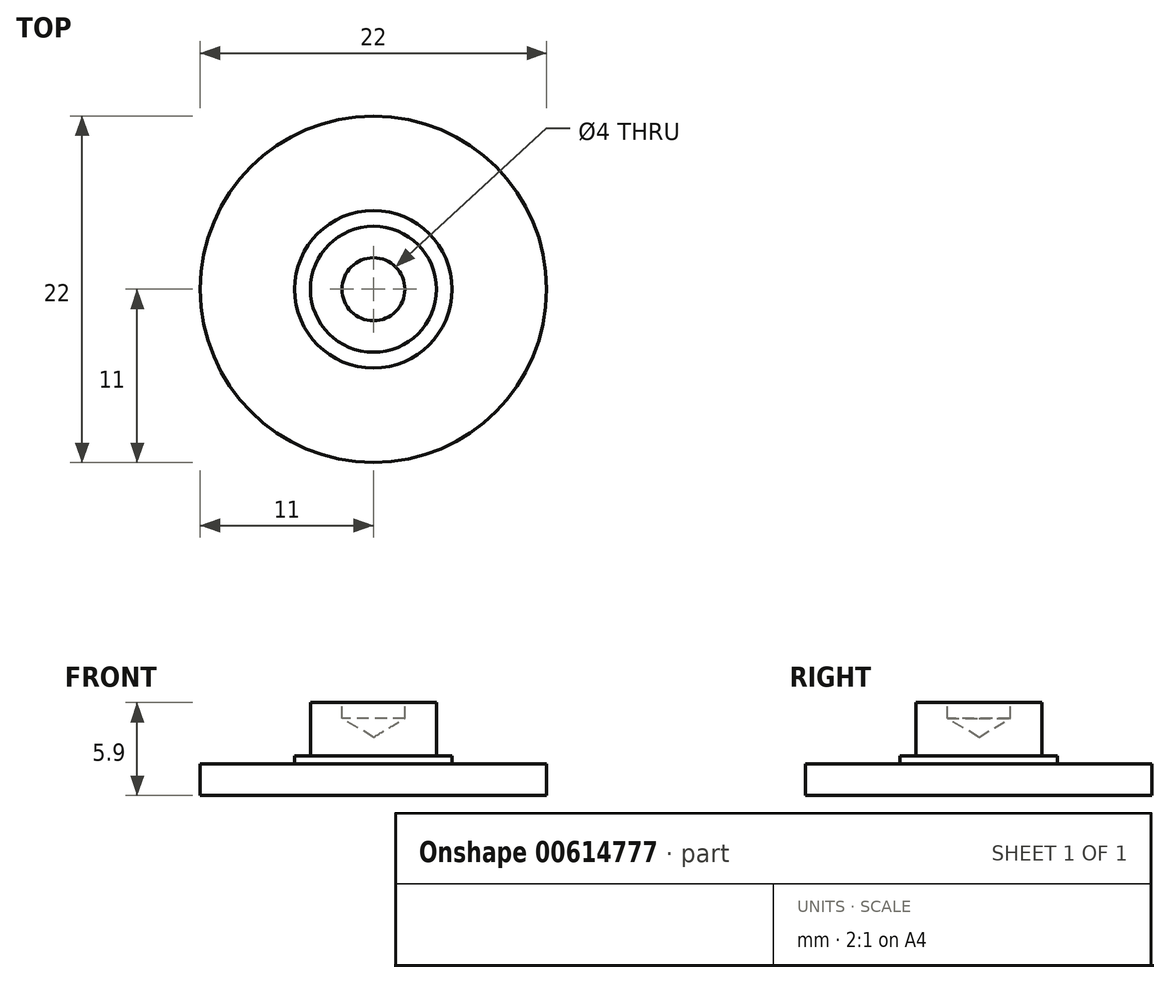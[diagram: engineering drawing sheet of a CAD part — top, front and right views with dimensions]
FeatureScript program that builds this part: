
annotation { "Feature Type Name" : "Feature", "Feature Type Description" : "" }
export const myFeature = defineFeature(function(context is Context, id is Id, definition is map)
    precondition{}
    {
        {
            var Q0;
            Q0=qCreatedBy(makeId("Top.planeOp"),FACE);
            var sketch = newSketch(context, id + "F0", { "sketchPlane" : qUnion([Q0])});
            skCircle(sketch, "E0", {"center": v(0, 0) * mm, "radius": 11 * mm});
            skSolve(sketch);
        }
        {
            var Q0;
            Q0=makeQuery(id+"F0.imprint","IMPRINT",FACE,{"disambiguationData":[TD([[makeQuery(id+"F0.imprint","IMPRINT",EDGE,{"derivedFrom":sQuery(id+"F0.wireOp",EDGE,"E0")}),1.0]])]});
            extrude(context, id + "F1", {"entities" : qUnion([Q0]), "depth" : 2 * mm, "offsetDistance" : 25 * mm});
        }
        {
            var Q0;
            Q0=makeQuery(id+"F1.opExtrude","CAP_FACE",FACE,{"disambiguationData":[OSD([sQuery(id+"F0.wireOp",EDGE,"E0")])],"isStart":false});
            var sketch = newSketch(context, id + "F2", { "sketchPlane" : qUnion([Q0])});
            skCircle(sketch, "E1", {"center": v(0, 0) * mm, "radius": 5 * mm});
            skSolve(sketch);
        }
        {
            var Q0;
            Q0=makeQuery(id+"F2.imprint","IMPRINT",FACE,{"disambiguationData":[TD([[makeQuery(id+"F2.imprint","IMPRINT",EDGE,{"derivedFrom":sQuery(id+"F2.wireOp",EDGE,"E1")}),1.0]])]});
            extrude(context, id + "F3", {"entities" : qUnion([Q0]), "operationType" : NewBodyOperationType.ADD, "depth" : 0.5 * mm, "offsetDistance" : 25 * mm});
        }
        {
            var Q0;
            Q0=makeQuery(id+"F3.opExtrude","CAP_FACE",FACE,{"disambiguationData":[OSD([sQuery(id+"F2.wireOp",EDGE,"E1")])],"isStart":false});
            var sketch = newSketch(context, id + "F4", { "sketchPlane" : qUnion([Q0])});
            skCircle(sketch, "E2", {"center": v(0, 0) * mm, "radius": 4 * mm});
            skSolve(sketch);
        }
        {
            var Q0;
            Q0=makeQuery(id+"F4.imprint","IMPRINT",FACE,{"disambiguationData":[TD([[makeQuery(id+"F4.imprint","IMPRINT",EDGE,{"derivedFrom":sQuery(id+"F4.wireOp",EDGE,"E2")}),1.0]])]});
            extrude(context, id + "F5", {"entities" : qUnion([Q0]), "operationType" : NewBodyOperationType.ADD, "depth" : 3.4 * mm, "offsetDistance" : 25 * mm});
        }
        {
            var Q0;
            Q0=makeQuery(id+"F5.opExtrude","CAP_FACE",FACE,{"disambiguationData":[OSD([sQuery(id+"F4.wireOp",EDGE,"E2")])],"isStart":false});
            var sketch = newSketch(context, id + "F6", { "sketchPlane" : qUnion([Q0])});
            skPoint(sketch, "E3", {"position": v(0, 0) * mm});
            skSolve(sketch);
        }
        {
            var Q0;
            Q0=sQuery(id+"F6.wireOp",VERTEX,"E3");
            var Q1;
            Q1=makeQuery(id+"F1.opExtrude","SWEPT_BODY",BODY,{"disambiguationData":[OSD([sQuery(id+"F0.wireOp",EDGE,"E0")])]});
            hole(context, id + "F7", {"style" : HoleStyle.SIMPLE, "endStyle" : HoleEndStyle.BLIND, "holeDiameter" : 4 * mm, "majorDiameter" : 5 * mm, "holeDepth" : 1 * mm, "isTappedThrough" : true, "tappedDepth" : 12 * mm, "tapClearance" : 3, "locations" : qUnion([Q0]), "scope" : qUnion([Q1])});
        }
    });
